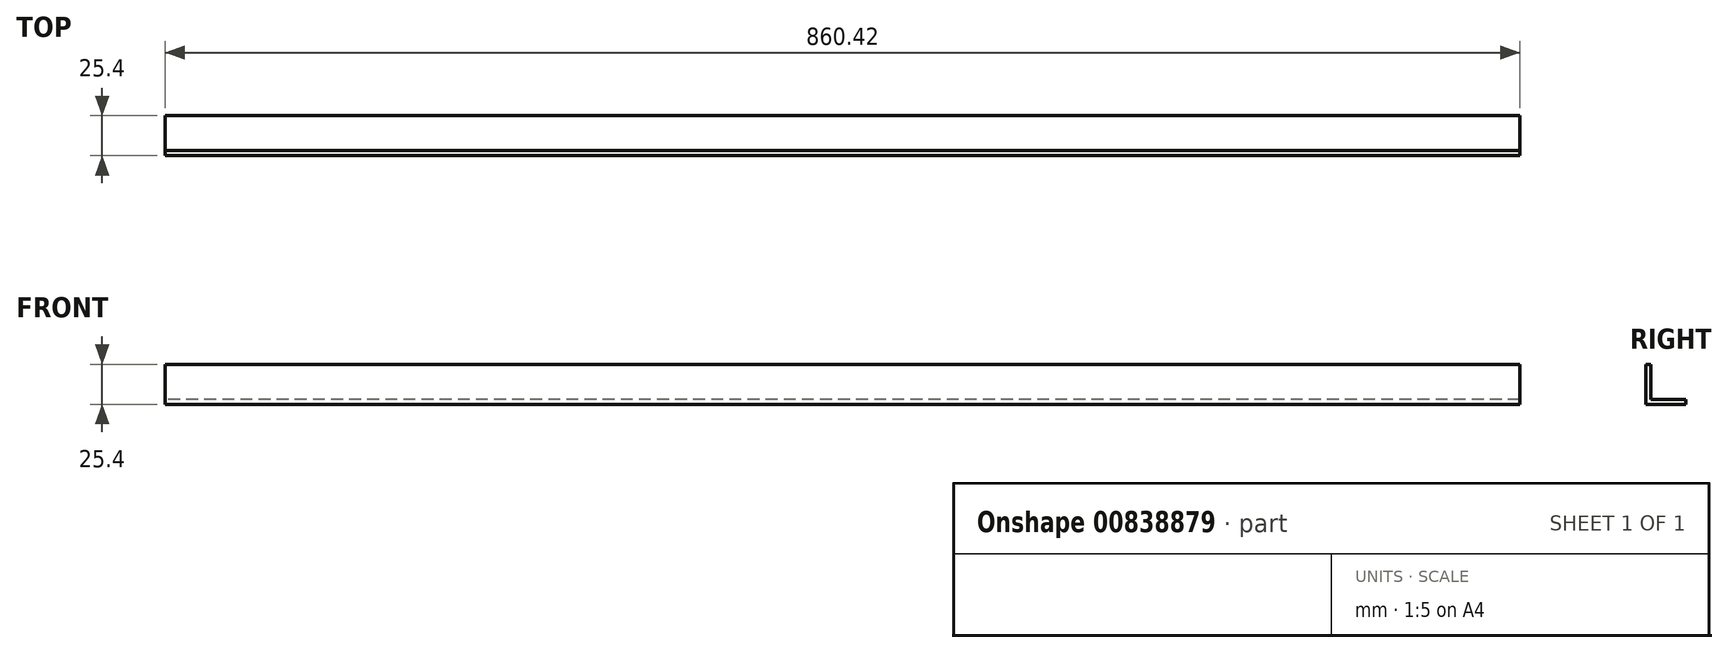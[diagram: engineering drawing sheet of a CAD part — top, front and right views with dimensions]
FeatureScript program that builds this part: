
annotation { "Feature Type Name" : "Feature", "Feature Type Description" : "" }
export const myFeature = defineFeature(function(context is Context, id is Id, definition is map)
    precondition{}
    {
        {
            var Q0;
            Q0=qCreatedBy(makeId("Right.planeOp"),FACE);
            var sketch = newSketch(context, id + "F0", { "sketchPlane" : qUnion([Q0])});
            skLineSegment(sketch, "E0", {"start": v(0, 0) * mm, "end": v(0, 25.4) * mm});
            skLineSegment(sketch, "E1", {"start": v(0, 25.4) * mm, "end": v(3.17, 25.4) * mm});
            skLineSegment(sketch, "E2", {"start": v(3.17, 25.4) * mm, "end": v(3.18, 3.17) * mm});
            skLineSegment(sketch, "E3", {"start": v(3.18, 3.17) * mm, "end": v(25.4, 3.18) * mm});
            skLineSegment(sketch, "E4", {"start": v(25.4, 3.18) * mm, "end": v(25.4, 0) * mm});
            skLineSegment(sketch, "E5", {"start": v(25.4, 0) * mm, "end": v(0, 0) * mm});
            skSolve(sketch);
        }
        {
            var Q0;
            Q0=makeQuery(id+"F0.imprint","IMPRINT",FACE,{"disambiguationData":[TD([[makeQuery(id+"F0.imprint","IMPRINT",EDGE,{"derivedFrom":sQuery(id+"F0.wireOp",EDGE,"E0")}),-1.0]])]});
            var Q1;
            Q1=makeQuery(id+"F0.imprint","IMPRINT",FACE,{"disambiguationData":[TD([[makeQuery(id+"F0.imprint","IMPRINT",EDGE,{"derivedFrom":sQuery(id+"F0.wireOp",EDGE,"E4")}),-1.0]])]});
            extrude(context, id + "F1", {"entities" : qUnion([Q0, Q1]), "depth" : 860.42 * mm, "offsetDistance" : 25.4 * mm});
        }
    });
